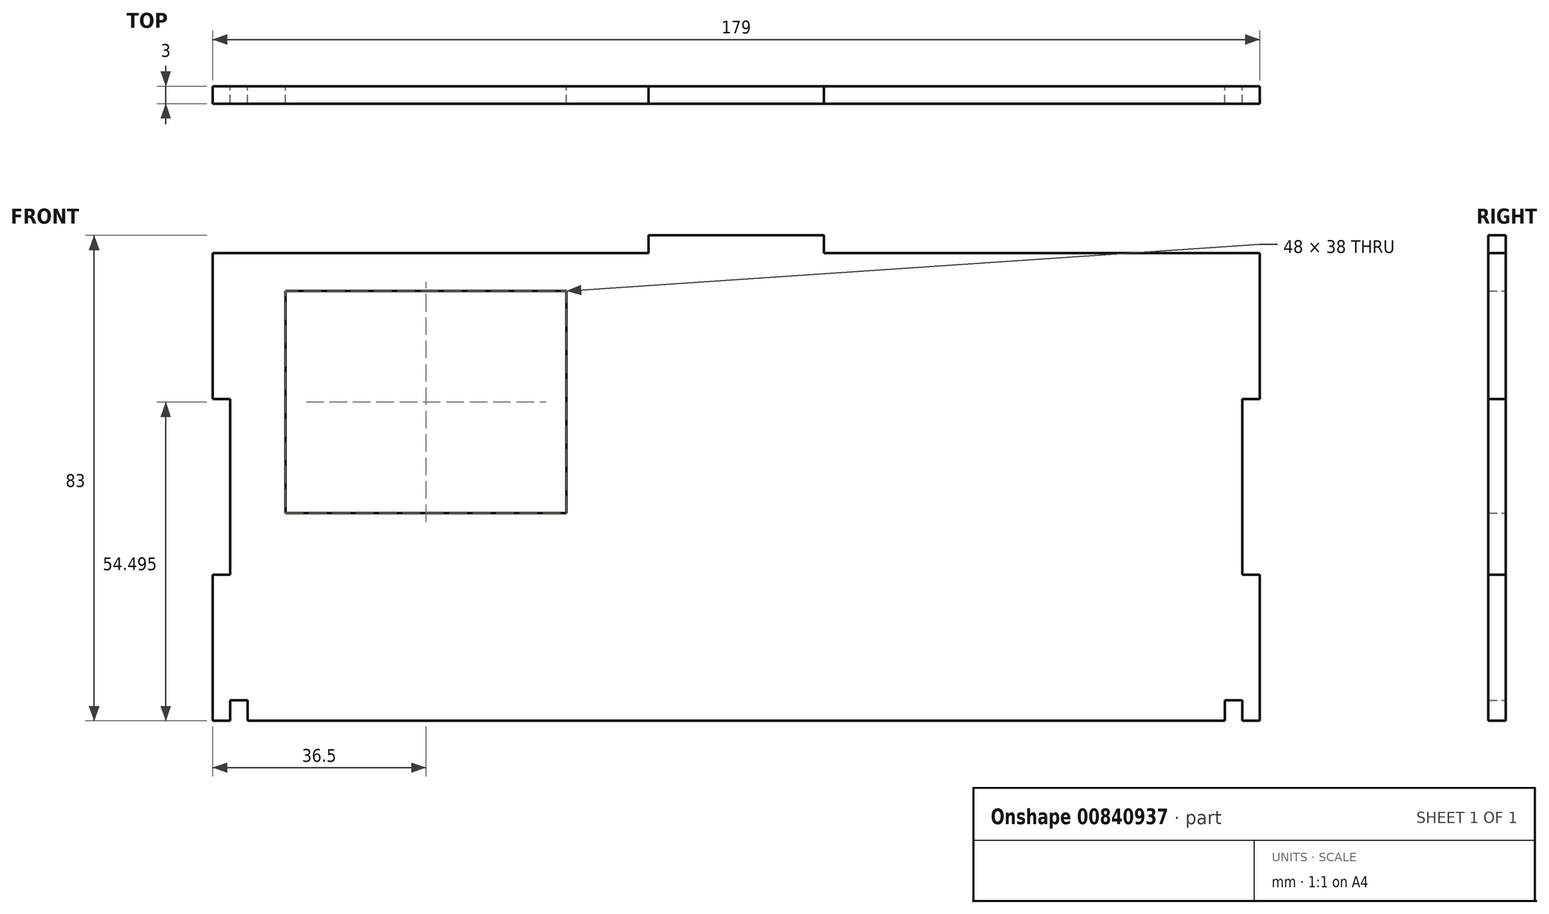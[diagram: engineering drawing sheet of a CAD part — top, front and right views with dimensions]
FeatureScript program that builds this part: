
annotation { "Feature Type Name" : "Feature", "Feature Type Description" : "" }
export const myFeature = defineFeature(function(context is Context, id is Id, definition is map)
    precondition{}
    {
        {
            var Q0;
            Q0=qCreatedBy(makeId("Front.planeOp"),FACE);
            var sketch = newSketch(context, id + "F0", { "sketchPlane" : qUnion([Q0])});
            skLineSegment(sketch, "E0.bottom", {"start": v(-112, 78.25) * mm, "end": v(-37.5, 78.25) * mm});
            skLineSegment(sketch, "E0.top", {"start": v(-112, -1.75) * mm, "end": v(67, -1.75) * mm});
            skLineSegment(sketch, "E0.left", {"start": v(-112, 78.25) * mm, "end": v(-112, -1.75) * mm});
            skLineSegment(sketch, "E0.right", {"start": v(67, 78.25) * mm, "end": v(67, -1.75) * mm});
            skLineSegment(sketch, "E1.bottom", {"start": v(-99.5, 71.75) * mm, "end": v(-51.5, 71.75) * mm});
            skLineSegment(sketch, "E1.top", {"start": v(-99.5, 33.75) * mm, "end": v(-51.5, 33.75) * mm});
            skLineSegment(sketch, "E1.left", {"start": v(-99.5, 71.75) * mm, "end": v(-99.5, 33.75) * mm});
            skLineSegment(sketch, "E1.right", {"start": v(-51.5, 71.75) * mm, "end": v(-51.5, 33.75) * mm});
            skLineSegment(sketch, "E2.bottom", {"start": v(-109, -1.75) * mm, "end": v(-106, -1.75) * mm});
            skLineSegment(sketch, "E2.top", {"start": v(-109, 1.75) * mm, "end": v(-106, 1.75) * mm});
            skLineSegment(sketch, "E2.left", {"start": v(-109, -1.75) * mm, "end": v(-109, 1.75) * mm});
            skLineSegment(sketch, "E2.right", {"start": v(-106, -1.75) * mm, "end": v(-106, 1.75) * mm});
            skLineSegment(sketch, "E3", {"start": v(-22.5, -1.75) * mm, "end": v(-22.5, 15.95) * mm, "construction": true});
            skLineSegment(sketch, "E4.MirrorCS", {"start": v(61, -1.75) * mm, "end": v(61, 1.75) * mm});
            skLineSegment(sketch, "E5.MirrorCS", {"start": v(64, 1.75) * mm, "end": v(61, 1.75) * mm});
            skLineSegment(sketch, "E6.MirrorCS", {"start": v(64, -1.75) * mm, "end": v(64, 1.75) * mm});
            skLineSegment(sketch, "E7.MirrorCS", {"start": v(64, -1.75) * mm, "end": v(61, -1.75) * mm});
            skLineSegment(sketch, "E8", {"start": v(-22.5, 78.25) * mm, "end": v(-22.5, 14.24) * mm, "construction": true});
            skLineSegment(sketch, "E9.bottom", {"start": v(-37.5, 81.25) * mm, "end": v(-7.5, 81.25) * mm});
            skLineSegment(sketch, "E9.left", {"start": v(-37.5, 81.25) * mm, "end": v(-37.5, 78.25) * mm});
            skLineSegment(sketch, "E9.right", {"start": v(-7.5, 81.25) * mm, "end": v(-7.5, 78.25) * mm});
            skLineSegment(sketch, "E10.trimOffspring", {"start": v(-7.5, 78.25) * mm, "end": v(67, 78.25) * mm});
            skSolve(sketch);
        }
        {
            var Q0;
            Q0=makeQuery(id+"F0.imprint","IMPRINT",FACE,{"disambiguationData":[TD([[makeQuery(id+"F0.imprint","IMPRINT",EDGE,{"derivedFrom":sQuery(id+"F0.wireOp",EDGE,"E0.bottom")}),-1.0]])]});
            extrude(context, id + "F1", {"entities" : qUnion([Q0]), "depth" : 3 * mm, "offsetDistance" : 25 * mm});
        }
        {
            var Q0;
            Q0=makeQuery(id+"F1.opExtrude","CAP_FACE",FACE,{"disambiguationData":[OSD([sQuery(id+"F0.wireOp",EDGE,"E0.bottom"),sQuery(id+"F0.wireOp",EDGE,"E0.top"),sQuery(id+"F0.wireOp",EDGE,"E0.left"),sQuery(id+"F0.wireOp",EDGE,"E0.right"),sQuery(id+"F0.wireOp",EDGE,"E1.bottom"),sQuery(id+"F0.wireOp",EDGE,"E1.top"),sQuery(id+"F0.wireOp",EDGE,"E1.left"),sQuery(id+"F0.wireOp",EDGE,"E1.right"),sQuery(id+"F0.wireOp",EDGE,"E2.top"),sQuery(id+"F0.wireOp",EDGE,"E2.left"),sQuery(id+"F0.wireOp",EDGE,"E2.right"),sQuery(id+"F0.wireOp",EDGE,"E6.MirrorCS"),sQuery(id+"F0.wireOp",EDGE,"E5.MirrorCS"),sQuery(id+"F0.wireOp",EDGE,"E4.MirrorCS")])],"isStart":true});
            var sketch = newSketch(context, id + "F2", { "sketchPlane" : qUnion([Q0])});
            skLineSegment(sketch, "E11", {"start": v(22.5, -21) * mm, "end": v(22.5, -1.75) * mm, "construction": true});
            skLineSegment(sketch, "E12.bottom", {"start": v(-67, 53.25) * mm, "end": v(-64, 53.25) * mm});
            skLineSegment(sketch, "E12.top", {"start": v(-67, 23.25) * mm, "end": v(-64, 23.25) * mm});
            skLineSegment(sketch, "E12.left", {"start": v(-67, 53.25) * mm, "end": v(-67, 23.25) * mm});
            skLineSegment(sketch, "E12.right", {"start": v(-64, 53.25) * mm, "end": v(-64, 23.25) * mm});
            skLineSegment(sketch, "E13.MirrorCS", {"start": v(112, 23.25) * mm, "end": v(109, 23.25) * mm});
            skLineSegment(sketch, "E14.MirrorCS", {"start": v(112, 53.25) * mm, "end": v(109, 53.25) * mm});
            skLineSegment(sketch, "E15.MirrorCS", {"start": v(112, 53.25) * mm, "end": v(112, 23.25) * mm});
            skLineSegment(sketch, "E16.MirrorCS", {"start": v(109, 53.25) * mm, "end": v(109, 23.25) * mm});
            skLineSegment(sketch, "E17", {"start": v(74.75, 78.25) * mm, "end": v(74.75, 59.23) * mm, "construction": true});
            skSolve(sketch);
        }
        {
            var Q0;
            Q0 = qSketchRegion(id + "F2", true);
            extrude(context, id + "F3", {"entities" : qUnion([Q0]), "operationType" : NewBodyOperationType.REMOVE, "oppositeDirection" : true, "depth" : 25 * mm, "offsetDistance" : 25 * mm});
        }
    });
